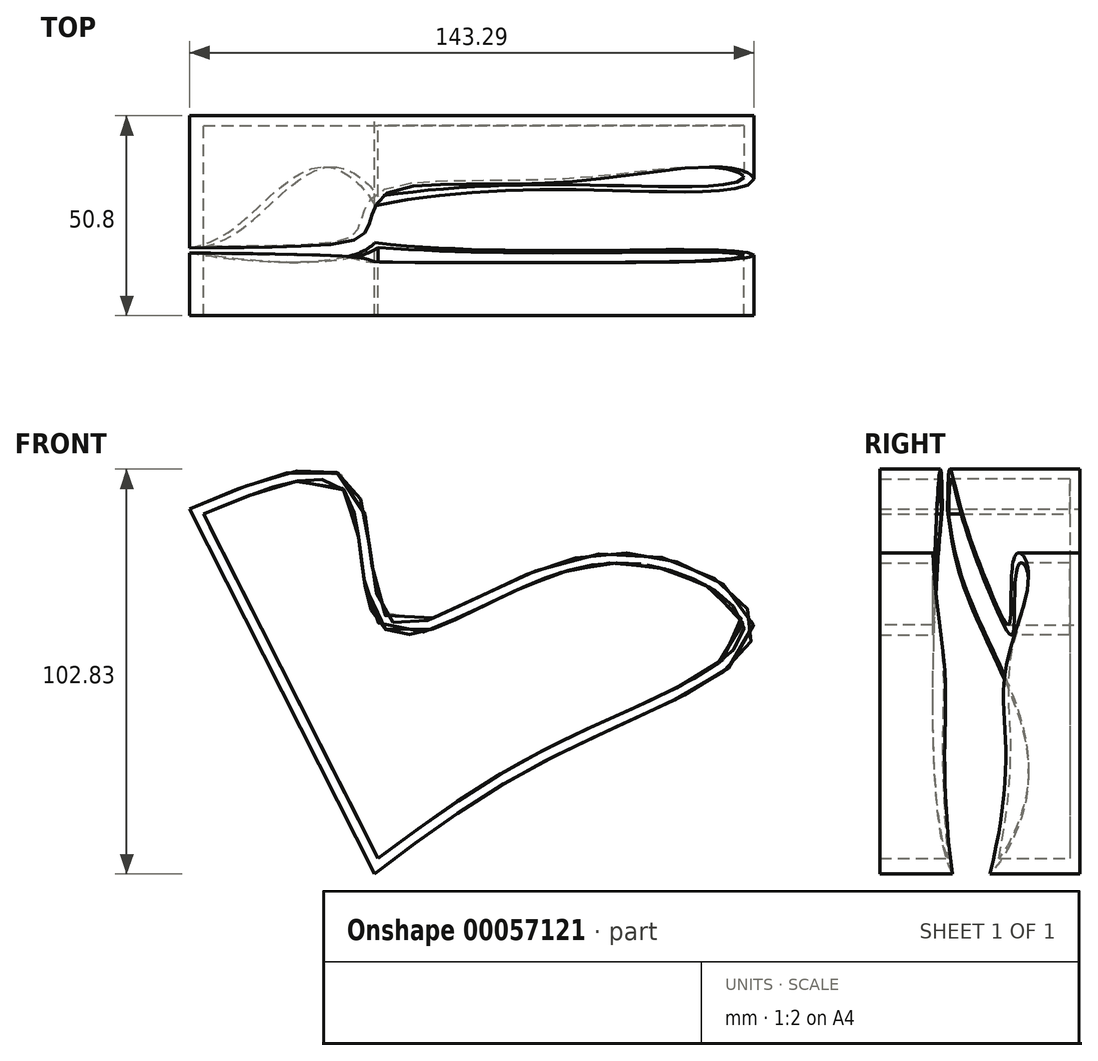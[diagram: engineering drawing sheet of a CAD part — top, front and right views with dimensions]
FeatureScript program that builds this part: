
annotation { "Feature Type Name" : "Feature", "Feature Type Description" : "" }
export const myFeature = defineFeature(function(context is Context, id is Id, definition is map)
    precondition{}
    {
        {
            var Q0;
            Q0=qCreatedBy(makeId("Front.planeOp"),FACE);
            var sketch = newSketch(context, id + "F0", { "sketchPlane" : qUnion([Q0])});
            skFitSpline(sketch, "E0", {"points": [v(-108.86, 25.65) * mm, v(-67.5, 31.97) * mm, v(-57.9, -2.65) * mm, v(-4.96, 14.28) * mm, v(34.41, -5.12) * mm, v(-12.57, -35.23) * mm, v(-61.88, -67) * mm], "startDerivative": vector(335.28, 144.4) * mm, "endDerivative": vector(-233.4, -177.23) * mm});
            skLineSegment(sketch, "E1", {"start": v(-108.86, 25.65) * mm, "end": v(-61.88, -67) * mm});
            skSolve(sketch);
        }
        {
            var Q0;
            Q0 = qSketchRegion(id + "F0", true);
            extrude(context, id + "F1", {"entities" : qUnion([Q0]), "depth" : 25.4 * mm});
        }
        {
            var Q0;
            Q0=makeQuery(id+"F1.opExtrude","CAP_FACE",FACE,{"disambiguationData":[OSD([sQuery(id+"F0.wireOp",EDGE,"E0"),sQuery(id+"F0.wireOp",EDGE,"E1")])],"isStart":false});
            extrude(context, id + "F2", {"entities" : qUnion([Q0]), "operationType" : NewBodyOperationType.ADD, "depth" : 25.4 * mm});
        }
        {
            var Q0;
            Q0=makeQuery(id+"F2.opExtrude","CAP_FACE",FACE,{"disambiguationData":[OSD([sQuery(id+"F0.wireOp",EDGE,"E0"),sQuery(id+"F0.wireOp",EDGE,"E1")])],"isStart":false});
            shell(context, id + "F3", {"entities" : qUnion([Q0]), "thickness" : 2.54 * mm});
        }
        {
            var Q0;
            {var subQ0=sQuery(id+"F0.wireOp",EDGE,"E1");Q0=makeQuery(id+"F2.boolean.opBoolean","MERGE",FACE,{"derivedFrom":[makeQuery(id+"F1.opExtrude","SWEPT_FACE",FACE,{"disambiguationData":[OSD([subQ0])]}),makeQuery(id+"F2.opExtrude","SWEPT_FACE",FACE,{"disambiguationData":[OSD([subQ0])]})]});}
            var sketch = newSketch(context, id + "F4", { "sketchPlane" : qUnion([Q0])});
            skSolve(sketch);
        }
        {
            var Q0;
            {var subQ0=sQuery(id+"F0.wireOp",EDGE,"E1");Q0=makeQuery(id+"F4.imprint","IMPRINT",FACE,{"disambiguationData":[TD([[makeQuery(id+"F4.imprint","IMPRINT",EDGE,{"derivedFrom":makeQuery(id+"F1.opExtrude","CAP_EDGE",EDGE,{"disambiguationData":[OSD([subQ0])],"isStart":true})}),1.0]])]});}
            var sketch = newSketch(context, id + "F5", { "sketchPlane" : qUnion([Q0])});
            skFitSpline(sketch, "E2", {"points": [v(30.77, 54.62) * mm, v(13.34, -8.6) * mm, v(30.97, -33.73) * mm, v(34.42, 75.9) * mm, v(30.77, 54.62) * mm]});
            skSolve(sketch);
        }
        {
            var Q0;
            Q0 = qSketchRegion(id + "F5", true);
            extrude(context, id + "F6", {"entities" : qUnion([Q0]), "operationType" : NewBodyOperationType.REMOVE, "endBound" : BoundingType.THROUGH_ALL, "oppositeDirection" : true, "depth" : 25.4 * mm});
        }
    });
